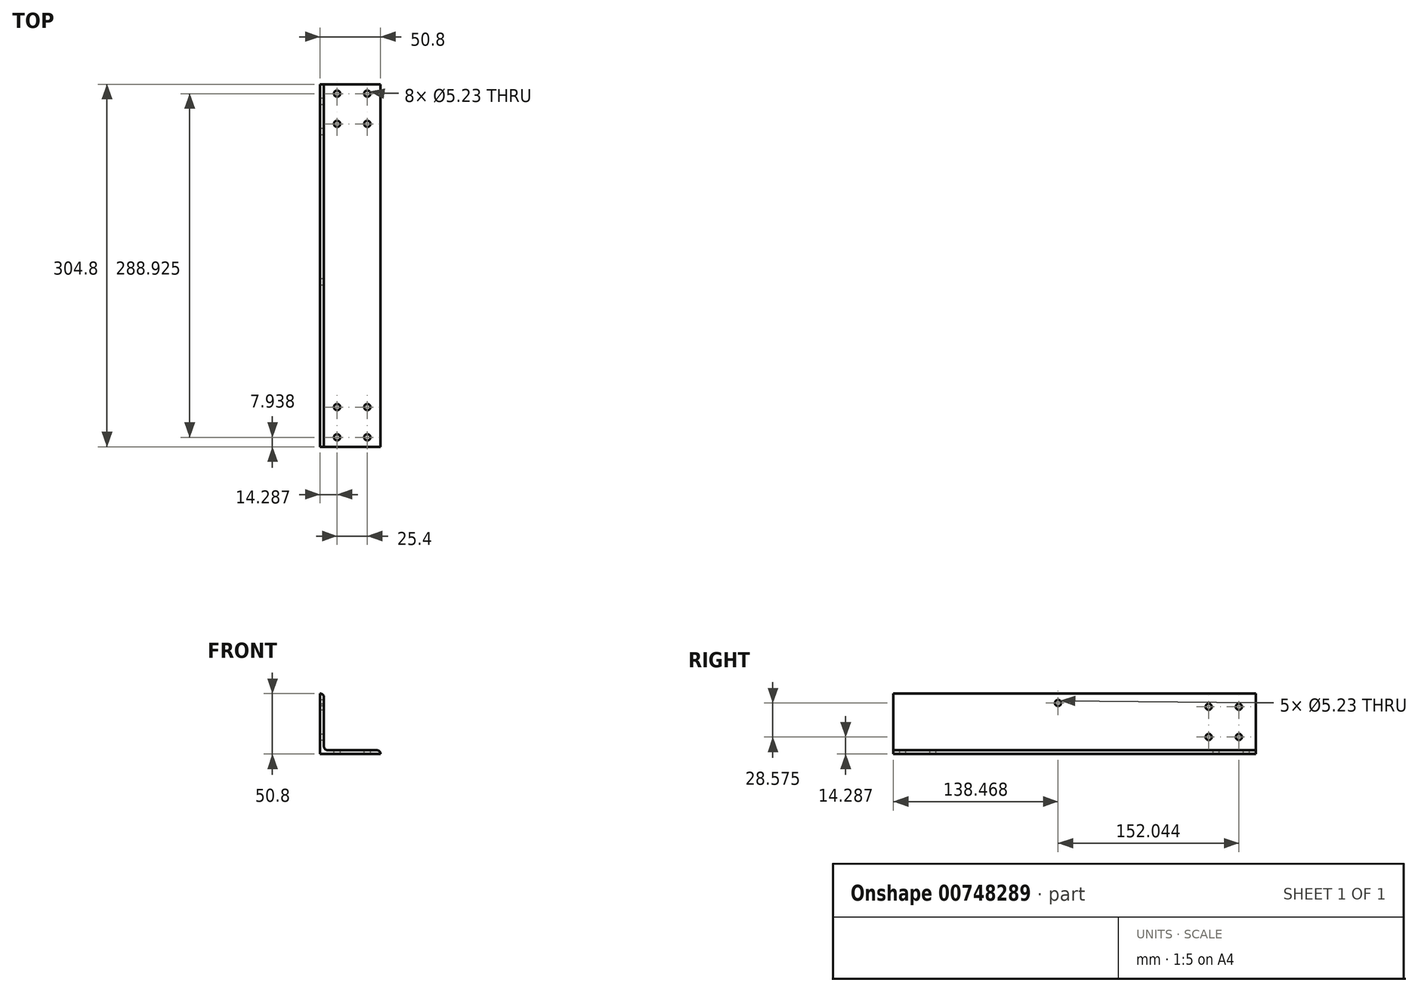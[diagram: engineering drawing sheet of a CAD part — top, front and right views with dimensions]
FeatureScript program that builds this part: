
annotation { "Feature Type Name" : "Feature", "Feature Type Description" : "" }
export const myFeature = defineFeature(function(context is Context, id is Id, definition is map)
    precondition{}
    {
        {
            var Q0;
            Q0=qCreatedBy(makeId("Front.planeOp"),FACE);
            var sketch = newSketch(context, id + "F0", { "sketchPlane" : qUnion([Q0])});
            skLineSegment(sketch, "E0", {"start": v(0, 0) * mm, "end": v(-50.8, 0) * mm});
            skLineSegment(sketch, "E1", {"start": v(-50.8, 0) * mm, "end": v(-50.8, 50.8) * mm});
            skLineSegment(sketch, "E2", {"start": v(-50.8, 50.8) * mm, "end": v(-50.8, 50.8) * mm});
            skLineSegment(sketch, "E3", {"start": v(-47.63, 47.63) * mm, "end": v(-47.63, 6.35) * mm});
            skLineSegment(sketch, "E4", {"start": v(-44.45, 3.18) * mm, "end": v(-3.18, 3.18) * mm});
            skLineSegment(sketch, "E5", {"start": v(0, 0) * mm, "end": v(0, 0) * mm});
            skPoint(sketch, "E6.visualSharp", {"position": v(-47.63, 3.18) * mm});
            skArc(sketch, "E6.filletArc", {"start": v(-47.63, 6.35) * mm, "mid": v(-46.7, 4.1) * mm, "end": v(-44.45, 3.18) * mm});
            skPoint(sketch, "E7.visualSharp", {"position": v(-47.63, 50.8) * mm});
            skArc(sketch, "E7.filletArc", {"start": v(-47.63, 47.63) * mm, "mid": v(-48.55, 49.87) * mm, "end": v(-50.8, 50.8) * mm});
            skPoint(sketch, "E8.visualSharp", {"position": v(0, 3.18) * mm});
            skArc(sketch, "E8.filletArc", {"start": v(0, 0) * mm, "mid": v(-0.93, 2.25) * mm, "end": v(-3.18, 3.18) * mm});
            skSolve(sketch);
        }
        {
            var Q0;
            Q0=qSketchRegion(id+"F0",true);
            extrude(context, id + "F1", {"entities" : qUnion([Q0]), "depth" : 304.8 * mm, "offsetDistance" : 25.4 * mm});
        }
        {
            var Q0;
            Q0=makeQuery(id+"F1.opExtrude","SWEPT_FACE",FACE,{"disambiguationData":[OSD([sQuery(id+"F0.wireOp",EDGE,"E3")])]});
            var sketch = newSketch(context, id + "F2", { "sketchPlane" : qUnion([Q0])});
            skLineSegment(sketch, "E9", {"start": v(-152.4, 6.35) * mm, "end": v(-152.4, 47.63) * mm, "construction": true});
            skLineSegment(sketch, "E10.0", {"start": v(-14.29, 6.35) * mm, "end": v(-14.29, 47.62) * mm, "construction": true});
            skLineSegment(sketch, "E11", {"start": v(-304.8, 26.99) * mm, "end": v(0, 26.99) * mm, "construction": true});
            skCircle(sketch, "E12", {"center": v(-14.29, 14.29) * mm, "radius": 2.62 * mm});
            skLineSegment(sketch, "E13", {"start": v(0, 14.29) * mm, "end": v(-304.8, 14.29) * mm, "construction": true});
            skLineSegment(sketch, "E14", {"start": v(-39.69, 47.63) * mm, "end": v(-39.69, 6.35) * mm, "construction": true});
            skCircle(sketch, "E15", {"center": v(-39.69, 14.29) * mm, "radius": 2.62 * mm});
            skLineSegment(sketch, "E16", {"start": v(0, 39.69) * mm, "end": v(-304.8, 39.69) * mm, "construction": true});
            skCircle(sketch, "E17", {"center": v(-14.29, 39.69) * mm, "radius": 2.62 * mm});
            skCircle(sketch, "E18", {"center": v(-39.69, 39.69) * mm, "radius": 2.62 * mm});
            skSolve(sketch);
        }
        {
            var Q0;
            Q0=qSketchRegion(id+"F2",true);
            extrude(context, id + "F3", {"entities" : qUnion([Q0]), "operationType" : NewBodyOperationType.REMOVE, "endBound" : BoundingType.THROUGH_ALL, "oppositeDirection" : true, "depth" : 25.4 * mm, "offsetDistance" : 25.4 * mm});
        }
        {
            var Q0;
            Q0=makeQuery(id+"F1.opExtrude","SWEPT_FACE",FACE,{"disambiguationData":[OSD([sQuery(id+"F0.wireOp",EDGE,"E4")])]});
            var sketch = newSketch(context, id + "F4", { "sketchPlane" : qUnion([Q0])});
            skLineSegment(sketch, "E19", {"start": v(-23.81, -304.8) * mm, "end": v(-23.81, 0) * mm, "construction": true});
            skLineSegment(sketch, "E20", {"start": v(-3.17, -296.86) * mm, "end": v(-44.45, -296.86) * mm, "construction": true});
            skCircle(sketch, "E21", {"center": v(-36.51, -296.86) * mm, "radius": 2.62 * mm});
            skLineSegment(sketch, "E22", {"start": v(-44.45, -7.94) * mm, "end": v(-3.18, -7.94) * mm, "construction": true});
            skCircle(sketch, "E23", {"center": v(-36.51, -7.94) * mm, "radius": 2.62 * mm});
            skLineSegment(sketch, "E24", {"start": v(-36.51, -304.8) * mm, "end": v(-36.51, 0) * mm, "construction": true});
            skLineSegment(sketch, "E25", {"start": v(-11.11, -304.8) * mm, "end": v(-11.11, -2.23) * mm, "construction": true});
            skCircle(sketch, "E26", {"center": v(-11.11, -7.94) * mm, "radius": 2.62 * mm});
            skCircle(sketch, "E27", {"center": v(-11.11, -296.86) * mm, "radius": 2.62 * mm});
            skLineSegment(sketch, "E28", {"start": v(-44.45, -271.46) * mm, "end": v(-3.17, -271.46) * mm, "construction": true});
            skCircle(sketch, "E29", {"center": v(-11.11, -271.46) * mm, "radius": 2.62 * mm});
            skCircle(sketch, "E30", {"center": v(-36.51, -271.46) * mm, "radius": 2.62 * mm});
            skLineSegment(sketch, "E31", {"start": v(-3.17, -33.34) * mm, "end": v(-44.45, -33.34) * mm, "construction": true});
            skCircle(sketch, "E32", {"center": v(-11.11, -33.34) * mm, "radius": 2.62 * mm});
            skCircle(sketch, "E33", {"center": v(-36.51, -33.34) * mm, "radius": 2.62 * mm});
            skSolve(sketch);
        }
        {
            var Q0;
            Q0=qSketchRegion(id+"F4",true);
            extrude(context, id + "F5", {"entities" : qUnion([Q0]), "operationType" : NewBodyOperationType.REMOVE, "endBound" : BoundingType.THROUGH_ALL, "oppositeDirection" : true, "depth" : 25.4 * mm, "offsetDistance" : 25.4 * mm});
        }
        {
            var Q0;
            Q0=makeQuery(id+"F1.opExtrude","SWEPT_FACE",FACE,{"disambiguationData":[OSD([sQuery(id+"F0.wireOp",EDGE,"E1")])]});
            var sketch = newSketch(context, id + "F6", { "sketchPlane" : qUnion([Q0])});
            skLineSegment(sketch, "E34", {"start": v(0, 42.86) * mm, "end": v(304.8, 42.86) * mm, "construction": true});
            skCircle(sketch, "E35", {"center": v(166.33, 42.86) * mm, "radius": 2.62 * mm});
            skSolve(sketch);
        }
        {
            var Q0;
            Q0 = qSketchRegion(id + "F6", true);
            extrude(context, id + "F7", {"entities" : qUnion([Q0]), "operationType" : NewBodyOperationType.REMOVE, "endBound" : BoundingType.THROUGH_ALL, "oppositeDirection" : true, "depth" : 25.4 * mm, "offsetDistance" : 25.4 * mm});
        }
    });
